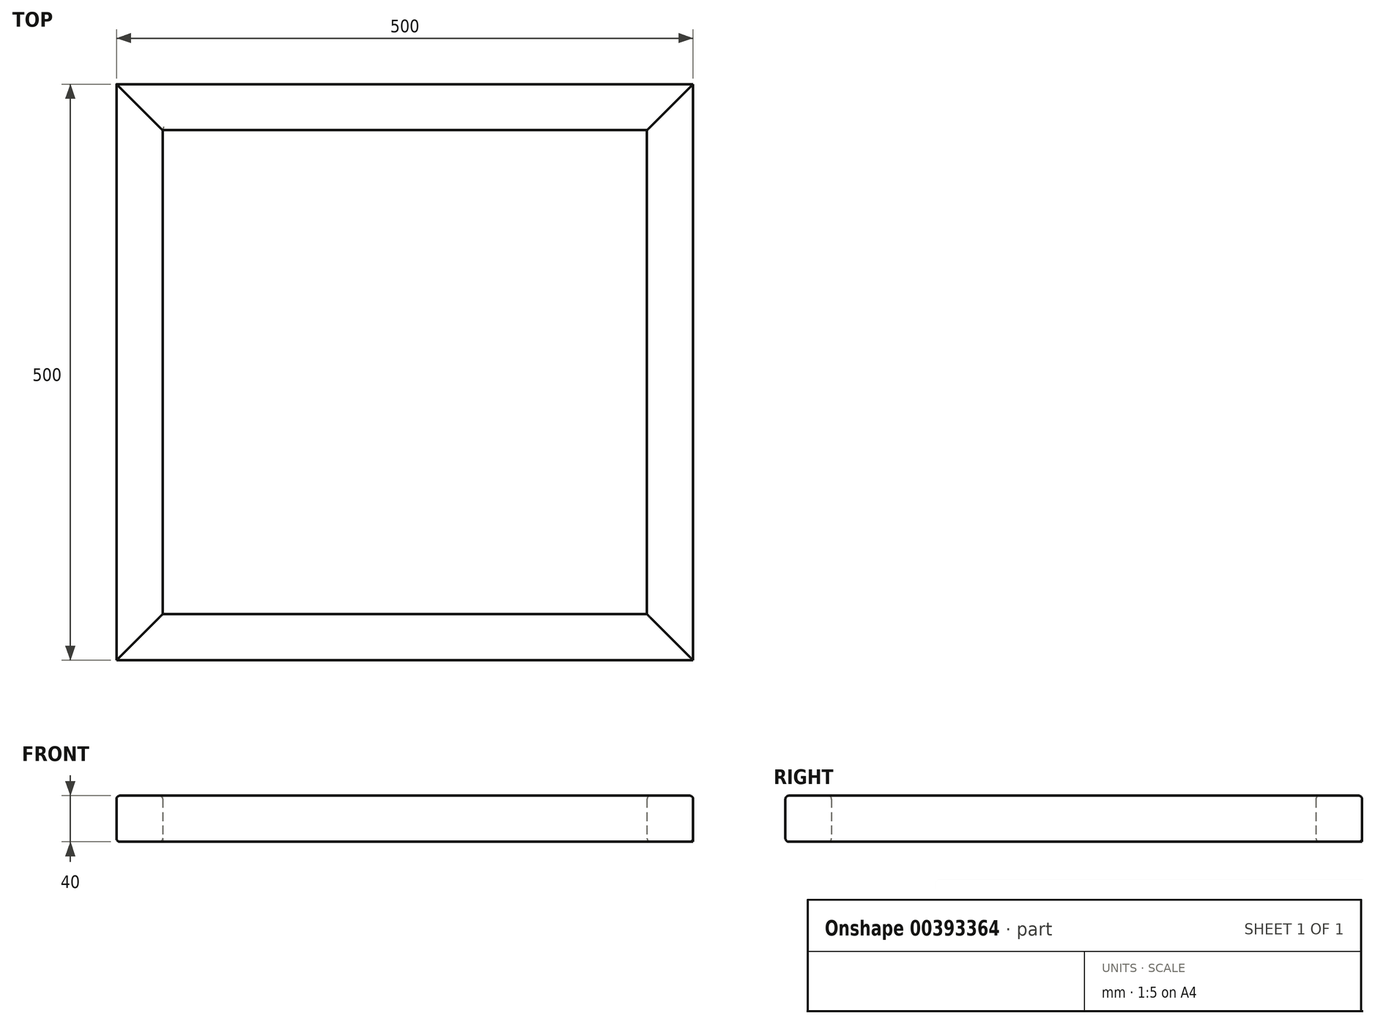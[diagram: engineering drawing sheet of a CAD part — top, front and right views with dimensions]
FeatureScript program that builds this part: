
annotation { "Feature Type Name" : "Feature", "Feature Type Description" : "" }
export const myFeature = defineFeature(function(context is Context, id is Id, definition is map)
    precondition{}
    {
        {
            var Q0;
            Q0=qCreatedBy(makeId("Top.planeOp"),FACE);
            var sketch = newSketch(context, id + "F0", { "sketchPlane" : qUnion([Q0])});
            skLineSegment(sketch, "E0", {"start": v(-250, 250) * mm, "end": v(250, 250) * mm});
            skLineSegment(sketch, "E1", {"start": v(-250, 250) * mm, "end": v(-210, 210) * mm});
            skLineSegment(sketch, "E2", {"start": v(-210, 210) * mm, "end": v(210, 210) * mm});
            skLineSegment(sketch, "E3", {"start": v(210, 210) * mm, "end": v(250, 250) * mm});
            skSolve(sketch);
        }
        {
            var Q0;
            Q0 = qSketchRegion(id + "F0", true);
            extrude(context, id + "F1", {"entities" : qUnion([Q0]), "depth" : 40 * mm, "offsetDistance" : 25 * mm});
        }
        {
            var Q0;
            Q0=makeQuery(id+"F1.opExtrude","CAP_EDGE",EDGE,{"disambiguationData":[OSD([sQuery(id+"F0.wireOp",EDGE,"E0")])],"isStart":false});
            var Q1;
            Q1=makeQuery(id+"F1.opExtrude","CAP_EDGE",EDGE,{"disambiguationData":[OSD([sQuery(id+"F0.wireOp",EDGE,"E2")])],"isStart":false});
            var Q2;
            Q2=makeQuery(id+"F1.opExtrude","CAP_EDGE",EDGE,{"disambiguationData":[OSD([sQuery(id+"F0.wireOp",EDGE,"E2")])],"isStart":true});
            var Q3;
            Q3=makeQuery(id+"F1.opExtrude","CAP_EDGE",EDGE,{"disambiguationData":[OSD([sQuery(id+"F0.wireOp",EDGE,"E1")])],"isStart":true});
            fillet(context, id + "F2", {"entities" : qUnion([Q0, Q1, Q2, Q3]), "radius" : 3 * mm, "tangentPropagation" : true, "allowEdgeOverflow" : false});
        }
        {
            var Q0;
            Q0=qCreatedBy(makeId("Top.planeOp"),FACE);
            var sketch = newSketch(context, id + "F3", { "sketchPlane" : qUnion([Q0])});
            skLineSegment(sketch, "E4", {"start": v(-250, 250) * mm, "end": v(-210, 210) * mm});
            skLineSegment(sketch, "E5", {"start": v(-250, 250) * mm, "end": v(-250, -250) * mm});
            skLineSegment(sketch, "E6", {"start": v(-210, 210) * mm, "end": v(-210, -210) * mm});
            skLineSegment(sketch, "E7", {"start": v(-210, -210) * mm, "end": v(-250, -250) * mm});
            skSolve(sketch);
        }
        {
            var Q0;
            Q0 = qSketchRegion(id + "F3", true);
            extrude(context, id + "F4", {"entities" : qUnion([Q0]), "depth" : 40 * mm, "offsetDistance" : 25 * mm});
        }
        {
            var Q0;
            Q0=makeQuery(id+"F4.opExtrude","CAP_EDGE",EDGE,{"disambiguationData":[OSD([sQuery(id+"F3.wireOp",EDGE,"E6")])],"isStart":false});
            var Q1;
            Q1=makeQuery(id+"F4.opExtrude","CAP_EDGE",EDGE,{"disambiguationData":[OSD([sQuery(id+"F3.wireOp",EDGE,"E6")])],"isStart":true});
            var Q2;
            Q2=makeQuery(id+"F4.opExtrude","CAP_EDGE",EDGE,{"disambiguationData":[OSD([sQuery(id+"F3.wireOp",EDGE,"E5")])],"isStart":false});
            var Q3;
            Q3=makeQuery(id+"F4.opExtrude","CAP_EDGE",EDGE,{"disambiguationData":[OSD([sQuery(id+"F3.wireOp",EDGE,"E5")])],"isStart":true});
            fillet(context, id + "F5", {"entities" : qUnion([Q0, Q1, Q2, Q3]), "radius" : 3 * mm, "tangentPropagation" : true, "allowEdgeOverflow" : false});
        }
        {
            var Q0;
            Q0=qCreatedBy(makeId("Top.planeOp"),FACE);
            var sketch = newSketch(context, id + "F6", { "sketchPlane" : qUnion([Q0])});
            skLineSegment(sketch, "E8", {"start": v(-250, -250) * mm, "end": v(-210, -210) * mm});
            skLineSegment(sketch, "E9", {"start": v(-210, -210) * mm, "end": v(210, -210) * mm});
            skLineSegment(sketch, "E10", {"start": v(210, -210) * mm, "end": v(250, -250) * mm});
            skLineSegment(sketch, "E11", {"start": v(250, -250) * mm, "end": v(-250, -250) * mm});
            skSolve(sketch);
        }
        {
            var Q0;
            Q0 = qSketchRegion(id + "F6", true);
            extrude(context, id + "F7", {"entities" : qUnion([Q0]), "depth" : 40 * mm, "offsetDistance" : 25 * mm});
        }
        {
            var Q0;
            Q0=makeQuery(id+"F7.opExtrude","CAP_EDGE",EDGE,{"disambiguationData":[OSD([sQuery(id+"F6.wireOp",EDGE,"E11")])],"isStart":false});
            var Q1;
            Q1=makeQuery(id+"F7.opExtrude","CAP_EDGE",EDGE,{"disambiguationData":[OSD([sQuery(id+"F6.wireOp",EDGE,"E9")])],"isStart":false});
            var Q2;
            Q2=makeQuery(id+"F7.opExtrude","CAP_EDGE",EDGE,{"disambiguationData":[OSD([sQuery(id+"F6.wireOp",EDGE,"E11")])],"isStart":true});
            var Q3;
            Q3=makeQuery(id+"F7.opExtrude","CAP_EDGE",EDGE,{"disambiguationData":[OSD([sQuery(id+"F6.wireOp",EDGE,"E9")])],"isStart":true});
            fillet(context, id + "F8", {"entities" : qUnion([Q0, Q1, Q2, Q3]), "radius" : 3 * mm, "tangentPropagation" : true, "allowEdgeOverflow" : false});
        }
        {
            var Q0;
            Q0=qCreatedBy(makeId("Top.planeOp"),FACE);
            var sketch = newSketch(context, id + "F9", { "sketchPlane" : qUnion([Q0])});
            skLineSegment(sketch, "E12", {"start": v(250, -250) * mm, "end": v(210, -210) * mm});
            skLineSegment(sketch, "E13", {"start": v(210, -210) * mm, "end": v(210, 210) * mm});
            skLineSegment(sketch, "E14", {"start": v(210, 210) * mm, "end": v(250, 250) * mm});
            skLineSegment(sketch, "E15", {"start": v(250, 250) * mm, "end": v(250, -250) * mm});
            skSolve(sketch);
        }
        {
            var Q0;
            Q0 = qSketchRegion(id + "F9", true);
            extrude(context, id + "F10", {"entities" : qUnion([Q0]), "depth" : 40 * mm, "offsetDistance" : 25 * mm});
        }
        {
            var Q0;
            Q0=makeQuery(id+"F10.opExtrude","CAP_EDGE",EDGE,{"disambiguationData":[OSD([sQuery(id+"F9.wireOp",EDGE,"E13")])],"isStart":false});
            var Q1;
            Q1=makeQuery(id+"F10.opExtrude","CAP_EDGE",EDGE,{"disambiguationData":[OSD([sQuery(id+"F9.wireOp",EDGE,"E15")])],"isStart":false});
            var Q2;
            Q2=makeQuery(id+"F10.opExtrude","CAP_EDGE",EDGE,{"disambiguationData":[OSD([sQuery(id+"F9.wireOp",EDGE,"E15")])],"isStart":true});
            var Q3;
            Q3=makeQuery(id+"F10.opExtrude","CAP_EDGE",EDGE,{"disambiguationData":[OSD([sQuery(id+"F9.wireOp",EDGE,"E13")])],"isStart":true});
            fillet(context, id + "F11", {"entities" : qUnion([Q0, Q1, Q2, Q3]), "radius" : 3 * mm, "tangentPropagation" : true, "allowEdgeOverflow" : false});
        }
    });
